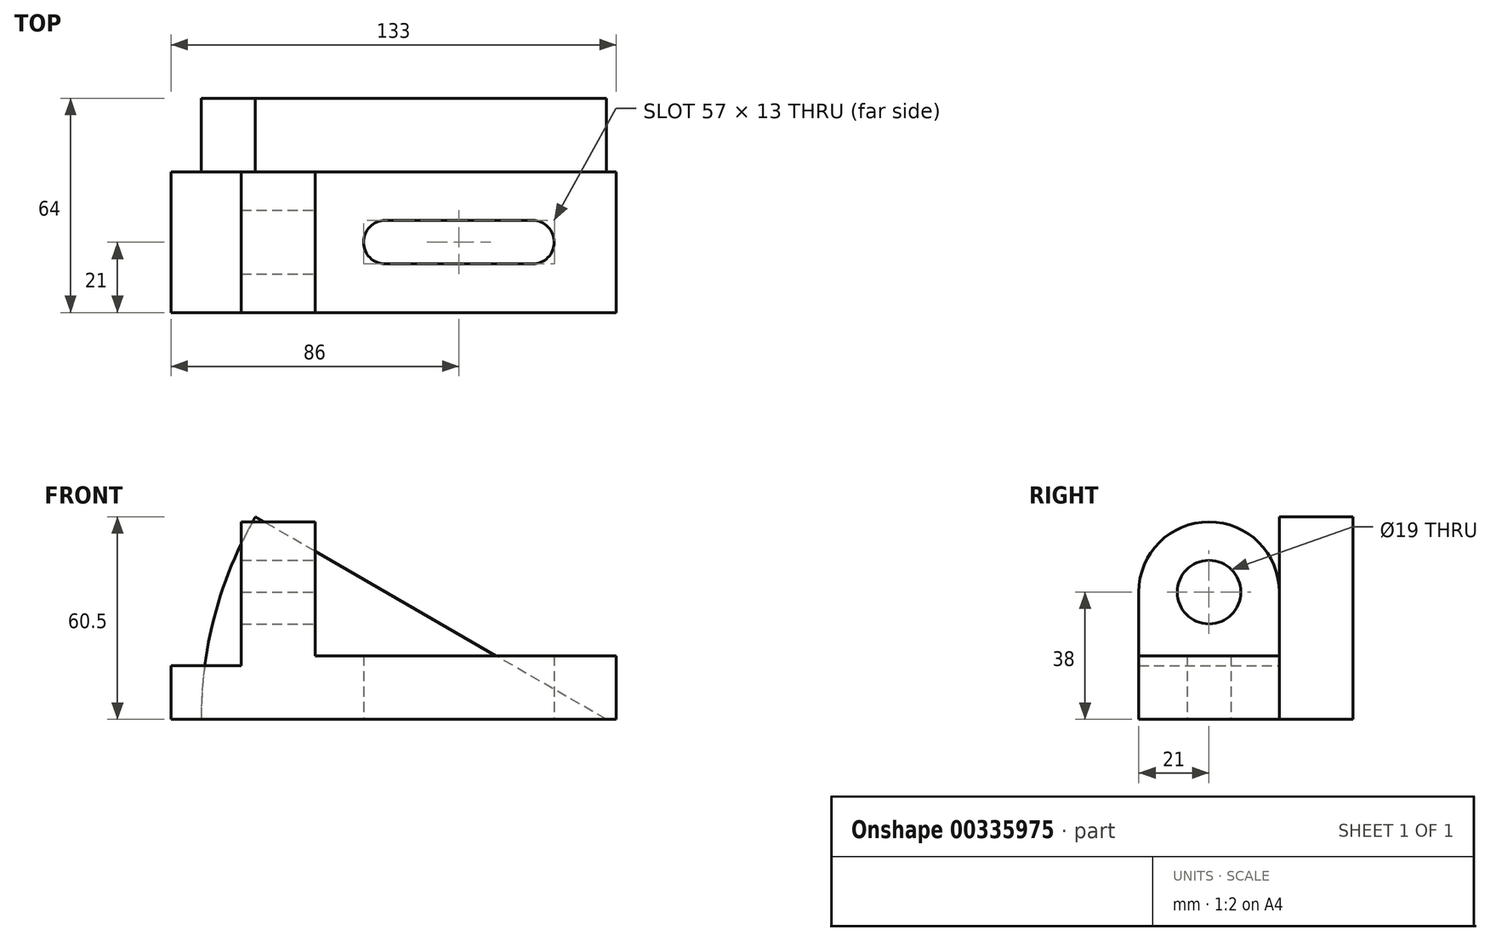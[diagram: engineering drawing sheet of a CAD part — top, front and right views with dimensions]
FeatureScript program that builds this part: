
annotation { "Feature Type Name" : "Feature", "Feature Type Description" : "" }
export const myFeature = defineFeature(function(context is Context, id is Id, definition is map)
    precondition{}
    {
        {
            var Q0;
            Q0=qCreatedBy(makeId("Front.planeOp"),FACE);
            var sketch = newSketch(context, id + "F0", { "sketchPlane" : qUnion([Q0])});
            skLineSegment(sketch, "E0", {"start": v(0, 0) * mm, "end": v(121, 0) * mm});
            skLineSegment(sketch, "E1", {"start": v(121, 0) * mm, "end": v(16.21, 60.5) * mm});
            skArc(sketch, "E2", {"start": v(16.21, 60.5) * mm, "mid": v(4.12, 31.32) * mm, "end": v(0, 0) * mm});
            skSolve(sketch);
        }
        {
            var Q0;
            Q0=makeQuery(id+"F0.imprint","IMPRINT",FACE,{"disambiguationData":[TD([[makeQuery(id+"F0.imprint","IMPRINT",EDGE,{"derivedFrom":sQuery(id+"F0.wireOp",EDGE,"E0")}),1.0]])]});
            extrude(context, id + "F1", {"entities" : qUnion([Q0]), "oppositeDirection" : true, "depth" : 22 * mm});
        }
        {
            var Q0;
            Q0=qCreatedBy(makeId("Front.planeOp"),FACE);
            var sketch = newSketch(context, id + "F2", { "sketchPlane" : qUnion([Q0])});
            skLineSegment(sketch, "E3", {"start": v(-9, 0) * mm, "end": v(124, 0) * mm});
            skLineSegment(sketch, "E4", {"start": v(-9, 0) * mm, "end": v(-9, 16) * mm});
            skLineSegment(sketch, "E5", {"start": v(-9, 16) * mm, "end": v(124, 16) * mm});
            skLineSegment(sketch, "E6", {"start": v(124, 16) * mm, "end": v(124, 0) * mm});
            skSolve(sketch);
        }
        {
            var Q0;
            Q0=makeQuery(id+"F2.imprint","IMPRINT",FACE,{"disambiguationData":[TD([[makeQuery(id+"F2.imprint","IMPRINT",EDGE,{"derivedFrom":sQuery(id+"F2.wireOp",EDGE,"E3")}),1.0]])]});
            extrude(context, id + "F3", {"entities" : qUnion([Q0]), "operationType" : NewBodyOperationType.ADD, "depth" : 42 * mm});
        }
        {
            var Q0;
            Q0=makeQuery(id+"F3.opExtrude","SWEPT_FACE",FACE,{"disambiguationData":[OSD([sQuery(id+"F2.wireOp",EDGE,"E5")])]});
            var sketch = newSketch(context, id + "F4", { "sketchPlane" : qUnion([Q0])});
            skLineSegment(sketch, "E7.bottom", {"start": v(12, 0) * mm, "end": v(34, 0) * mm});
            skLineSegment(sketch, "E7.top", {"start": v(12, -42) * mm, "end": v(34, -42) * mm});
            skLineSegment(sketch, "E7.left", {"start": v(12, 0) * mm, "end": v(12, -42) * mm});
            skLineSegment(sketch, "E7.right", {"start": v(34, 0) * mm, "end": v(34, -42) * mm});
            skSolve(sketch);
        }
        {
            var Q0;
            Q0=makeQuery(id+"F4.imprint","IMPRINT",FACE,{"disambiguationData":[TD([[makeQuery(id+"F4.imprint","IMPRINT",EDGE,{"derivedFrom":sQuery(id+"F4.wireOp",EDGE,"E7.bottom")}),-1.0]])]});
            extrude(context, id + "F5", {"entities" : qUnion([Q0]), "operationType" : NewBodyOperationType.ADD, "depth" : 22 * mm});
        }
        {
            var Q0;
            Q0=makeQuery(id+"F5.opExtrude","SWEPT_FACE",FACE,{"disambiguationData":[OSD([sQuery(id+"F4.wireOp",EDGE,"E7.right")])]});
            var sketch = newSketch(context, id + "F6", { "sketchPlane" : qUnion([Q0])});
            skCircle(sketch, "E8", {"center": v(-21, 38) * mm, "radius": 9.5 * mm});
            skArc(sketch, "E9", {"start": v(0, 38) * mm, "mid": v(-21, 59) * mm, "end": v(-42, 38) * mm});
            skSolve(sketch);
        }
        {
            var Q0;
            {var subQ5=sQuery(id+"F6.wireOp",EDGE,"E9");Q0=makeQuery(id+"F6.imprint","IMPRINT",FACE,{"disambiguationData":[TD([[makeQuery(id+"F6.imprint","IMPRINT",EDGE,{"derivedFrom":subQ5}),1.0]])]});}
            var Q1;
            Q1=makeQuery(id+"F5.opExtrude","SWEPT_FACE",FACE,{"disambiguationData":[OSD([sQuery(id+"F4.wireOp",EDGE,"E7.left")])]});
            extrude(context, id + "F7", {"entities" : qUnion([Q0]), "operationType" : NewBodyOperationType.ADD, "endBound" : BoundingType.UP_TO_SURFACE, "oppositeDirection" : true, "endBoundEntityFace" : qUnion([Q1]), "depth" : 25 * mm});
        }
        {
            var Q0;
            {var subQ0=sQuery(id+"F6.wireOp",EDGE,"E8");var subQ1=makeQuery(id+"F5.opExtrude","CAP_EDGE",EDGE,{"disambiguationData":[OSD([sQuery(id+"F4.wireOp",EDGE,"E7.right")])],"isStart":false});var subQ2=makeQuery(id+"F6.imprint","INTERSECT",VERTEX,{"disambiguationData":[OD(0.0)],"derivedFrom":[subQ1,subQ0]});Q0=makeQuery(id+"F6.imprint","IMPRINT",FACE,{"disambiguationData":[TD([[makeQuery(id+"F6.imprint","IMPRINT",EDGE,{"disambiguationData":[TD([[subQ2,-1.0]])],"derivedFrom":subQ0}),1.0]])]});}
            extrude(context, id + "F8", {"entities" : qUnion([Q0]), "operationType" : NewBodyOperationType.REMOVE, "endBound" : BoundingType.THROUGH_ALL, "oppositeDirection" : true, "depth" : 25 * mm});
        }
        {
            var Q0;
            {var subQ1=sQuery(id+"F2.wireOp",EDGE,"E5");var subQ4=sQuery(id+"F0.wireOp",EDGE,"E1");Q0=makeQuery(id+"F5.boolean.opBoolean","SPLIT",FACE,{"disambiguationData":[TD([makeQuery(id+"F1.opExtrude","SWEPT_FACE",FACE,{"disambiguationData":[OSD([subQ4])]})])],"derivedFrom":makeQuery(id+"F3.opExtrude","SWEPT_FACE",FACE,{"disambiguationData":[OSD([subQ1])]})});}
            var sketch = newSketch(context, id + "F9", { "sketchPlane" : qUnion([Q0])});
            skLineSegment(sketch, "E10", {"start": v(55, -21) * mm, "end": v(99, -21) * mm, "construction": true});
            skArc(sketch, "E11.0.startCap", {"start": v(55, -27.5) * mm, "mid": v(48.5, -21) * mm, "end": v(55, -14.5) * mm});
            skArc(sketch, "E11.0.endCap", {"start": v(99, -14.5) * mm, "mid": v(105.5, -21) * mm, "end": v(99, -27.5) * mm});
            skLineSegment(sketch, "E11.0.left", {"start": v(55, -14.5) * mm, "end": v(99, -14.5) * mm});
            skLineSegment(sketch, "E11.0.right", {"start": v(55, -27.5) * mm, "end": v(99, -27.5) * mm});
            skArc(sketch, "E12.0.startCap", {"start": v(55, -24.25) * mm, "mid": v(51.75, -21) * mm, "end": v(55, -17.75) * mm});
            skArc(sketch, "E12.0.endCap", {"start": v(99, -17.75) * mm, "mid": v(102.25, -21) * mm, "end": v(99, -24.25) * mm});
            skLineSegment(sketch, "E12.0.left", {"start": v(55, -17.75) * mm, "end": v(99, -17.75) * mm});
            skLineSegment(sketch, "E12.0.right", {"start": v(55, -24.25) * mm, "end": v(99, -24.25) * mm});
            skSolve(sketch);
        }
        {
            var Q0;
            Q0=makeQuery(id+"F9.imprint","IMPRINT",FACE,{"disambiguationData":[TD([[makeQuery(id+"F9.imprint","IMPRINT",EDGE,{"derivedFrom":sQuery(id+"F9.wireOp",EDGE,"E11.0.startCap")}),-1.0]])]});
            extrude(context, id + "F10", {"entities" : qUnion([Q0]), "operationType" : NewBodyOperationType.ADD, "depth" : 3 * mm});
        }
        {
            var Q0;
            {var subQ1=sQuery(id+"F2.wireOp",EDGE,"E5");var subQ4=sQuery(id+"F0.wireOp",EDGE,"E1");Q0=makeQuery(id+"F10.boolean.opBoolean","SPLIT",FACE,{"disambiguationData":[TD([makeQuery(id+"F10.opExtrude","SWEPT_FACE",FACE,{"disambiguationData":[OSD([sQuery(id+"F9.wireOp",EDGE,"E12.0.startCap")])]})])],"derivedFrom":makeQuery(id+"F5.boolean.opBoolean","SPLIT",FACE,{"disambiguationData":[TD([makeQuery(id+"F1.opExtrude","SWEPT_FACE",FACE,{"disambiguationData":[OSD([subQ4])]})])],"derivedFrom":makeQuery(id+"F3.opExtrude","SWEPT_FACE",FACE,{"disambiguationData":[OSD([subQ1])]})})});}
            extrude(context, id + "F11", {"entities" : qUnion([Q0]), "operationType" : NewBodyOperationType.REMOVE, "endBound" : BoundingType.THROUGH_ALL, "oppositeDirection" : true, "depth" : 25 * mm});
        }
    });
